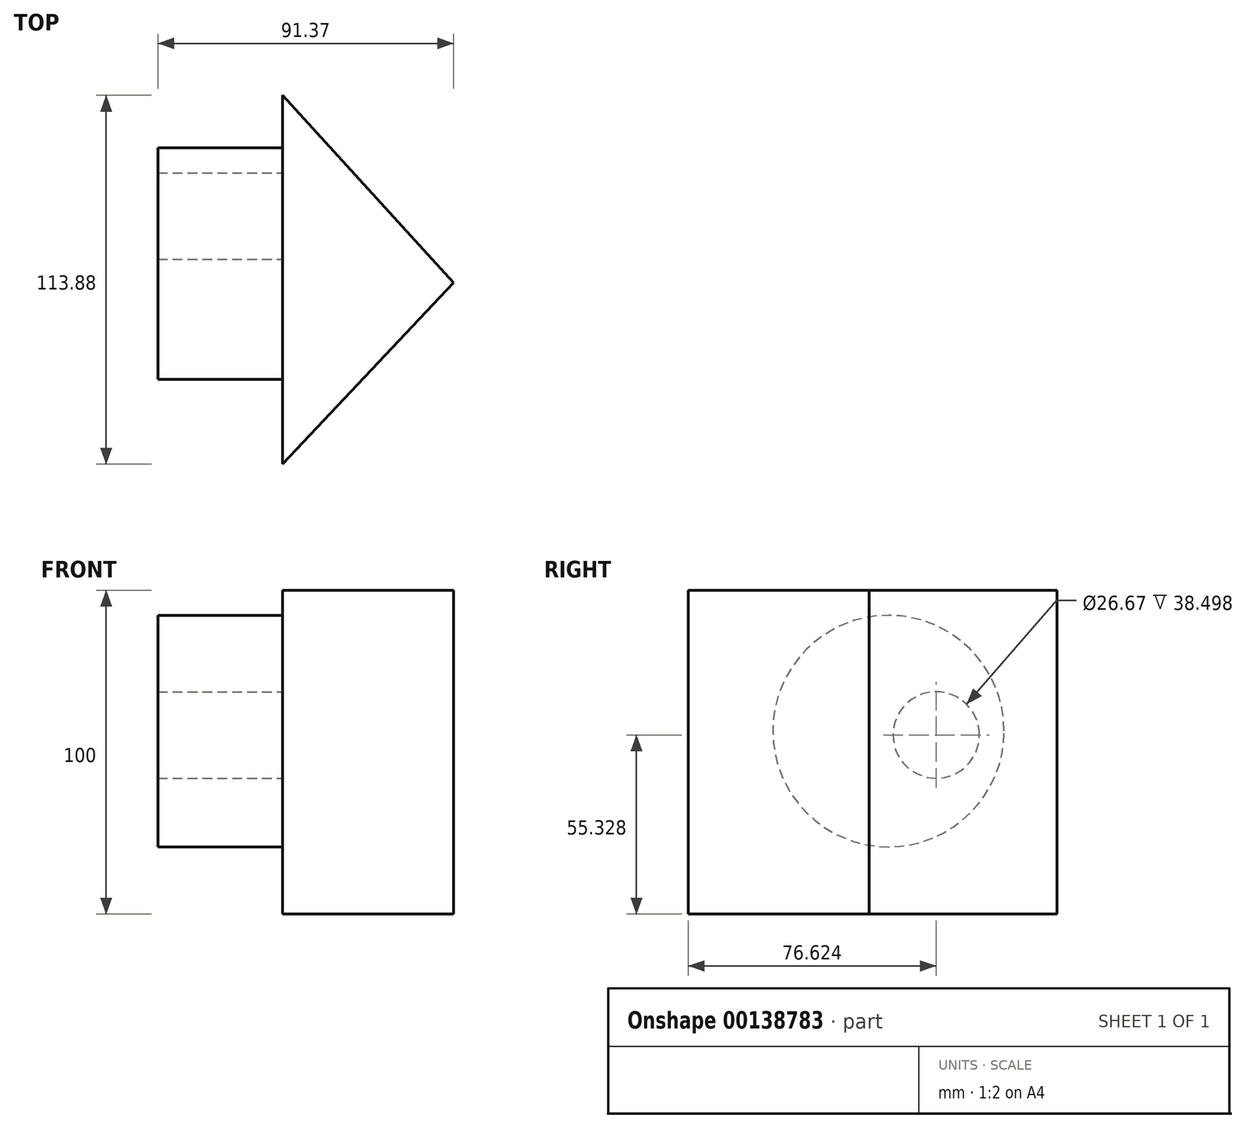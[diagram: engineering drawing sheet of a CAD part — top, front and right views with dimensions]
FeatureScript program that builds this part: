
annotation { "Feature Type Name" : "Feature", "Feature Type Description" : "" }
export const myFeature = defineFeature(function(context is Context, id is Id, definition is map)
    precondition{}
    {
        {
            var Q0;
            Q0=qCreatedBy(makeId("Top.planeOp"),FACE);
            var sketch = newSketch(context, id + "F0", { "sketchPlane" : qUnion([Q0])});
            skLineSegment(sketch, "E0", {"start": v(-52.87, -55.95) * mm, "end": v(-52.87, 57.93) * mm});
            skLineSegment(sketch, "E1", {"start": v(0, 0) * mm, "end": v(-52.87, -55.95) * mm});
            skLineSegment(sketch, "E2", {"start": v(-52.87, 57.93) * mm, "end": v(0, 0) * mm});
            skSolve(sketch);
        }
        {
            var Q0;
            Q0 = qSketchRegion(id + "F0", true);
            extrude(context, id + "F1", {"entities" : qUnion([Q0]), "depth" : 100 * mm});
        }
        {
            var Q0;
            Q0=makeQuery(id+"F1.opExtrude","SWEPT_FACE",FACE,{"disambiguationData":[OSD([sQuery(id+"F0.wireOp",EDGE,"E0")])]});
            var sketch = newSketch(context, id + "F2", { "sketchPlane" : qUnion([Q0])});
            skCircle(sketch, "E3", {"center": v(-20.67, 55.33) * mm, "radius": 13.34 * mm});
            skCircle(sketch, "E4", {"center": v(-5.93, 56.53) * mm, "radius": 35.74 * mm});
            skSolve(sketch);
        }
        {
            var Q0;
            Q0 = qSketchRegion(id + "F2", true);
            extrude(context, id + "F3", {"entities" : qUnion([Q0]), "operationType" : NewBodyOperationType.ADD, "depth" : 38.5 * mm});
        }
    });
